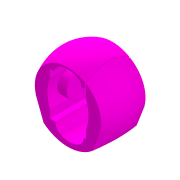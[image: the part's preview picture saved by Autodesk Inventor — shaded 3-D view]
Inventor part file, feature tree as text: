
AUTODESK INVENTOR PART (.ipt)
format: ipt  version: 2020 (Build 240168000, 168)  size: 811,008 bytes
history: native  units: mm
features: sketch x6, plane x3, extrude x3, other x3, loft x1, direct_edit x1, projected_geometry x1
ambient origin geometry x8: Origin, YZ Plane, XZ Plane, XY Plane, X Axis, Y Axis, Z Axis, Center Point
bodies: Solid1 (feature_tree)
feature tree (18):
  sketch  "Sketch1"  dims[d16=4.5mm d17=4.5mm]
  plane  "Work Plane1"
  sketch  "Sketch2"  dims[d19=0.0mm d20=90.0deg d21=0.0mm d22=90.0deg]
  plane  "Work Plane2"
  loft  "Loft1"
  extrude  "Extrusion1"  TaperAngle=0.0deg  [1 undecoded]
  plane  "Work Plane3"
  extrude  "Extrusion2"  Depth=0.2mm
  extrude  "Extrusion3"  Depth=10.0mm
  direct_edit  "Direct Edit1"
  other  "Image1"
  sketch  "Sketch3"  dims[d23=0.0mm d24=90.0deg d32=0.2mm]
  sketch  "Sketch4"  dims[d34=10.0mm d35=0.0mm d36=5.0mm]
  other  "Image2"
  sketch  "Sketch5"  dims[d37=10.0mm d38=0.0mm]
  projected_geometry  "Projected Loop1"
  sketch  "Sketch6"  dims[d39=4.5mm d40=0.0mm d41=8.0mm d42=10.0mm d43=10.0mm d33=0.5mm]
  other  "Scale1"
note: 1 required parameter value undecoded (feature->parameter linkage not recoverable at this tier; creation-order binding heuristic only, values carry confidence <= 0.55)
